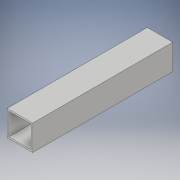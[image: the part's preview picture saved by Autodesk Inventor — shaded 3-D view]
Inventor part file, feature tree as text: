
AUTODESK INVENTOR PART (.ipt)
format: ipt  version: 2018 (Build 220112000, 112)  size: 97,280 bytes
history: native  units: in
note: dims shown in document units (in); Inventor stores cm internally (conversion verified against a paired STEP export)
features: extrude x1, sketch x1
ambient origin geometry x8: Origin, YZ Plane, XZ Plane, XY Plane, X Axis, Y Axis, Z Axis, Center Point
bodies: Solid1 (feature_tree)
feature tree (2):
  extrude  "Extrusion1"  Depth=1.0in
  sketch  "Sketch1"  dims[d0=1.0in d1=1.0in d2=0.0625in d3=0.0625in d4=0.0625in d5=0.0625in d6=5.5in d7=0.0in]
